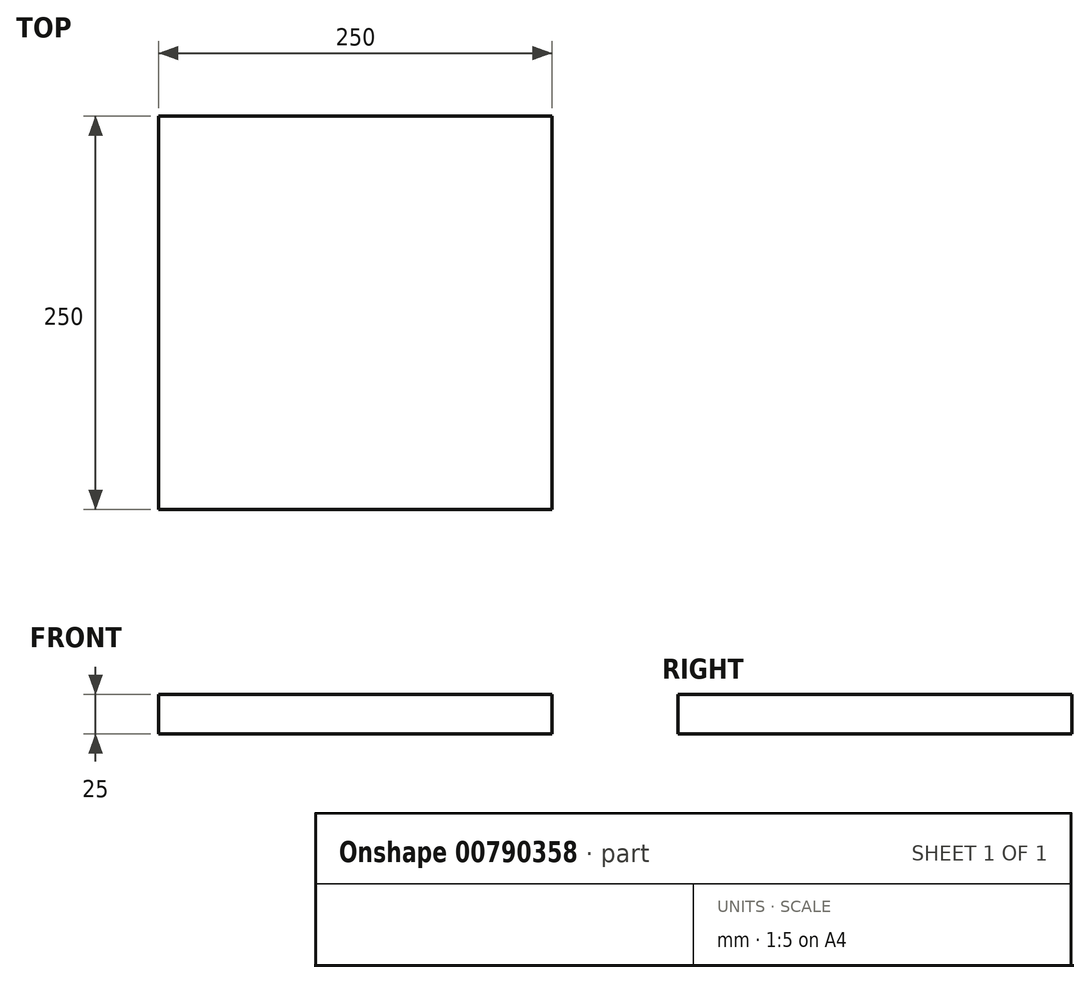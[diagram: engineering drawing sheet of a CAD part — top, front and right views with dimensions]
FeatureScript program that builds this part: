
annotation { "Feature Type Name" : "Feature", "Feature Type Description" : "" }
export const myFeature = defineFeature(function(context is Context, id is Id, definition is map)
    precondition{}
    {
        {
            var Q0;
            Q0=qCreatedBy(makeId("Top.planeOp"),FACE);
            var sketch = newSketch(context, id + "F0", { "sketchPlane" : qUnion([Q0])});
            skLineSegment(sketch, "E0.bottom", {"start": v(125, 125) * mm, "end": v(-125, 125) * mm});
            skLineSegment(sketch, "E0.top", {"start": v(125, -125) * mm, "end": v(-125, -125) * mm});
            skLineSegment(sketch, "E0.left", {"start": v(125, 125) * mm, "end": v(125, -125) * mm});
            skLineSegment(sketch, "E0.right", {"start": v(-125, 125) * mm, "end": v(-125, -125) * mm});
            skPoint(sketch, "E0.middle", {"position": v(0, 0) * mm});
            skSolve(sketch);
        }
        {
            var Q0;
            Q0 = qSketchRegion(id + "F0", true);
            extrude(context, id + "F1", {"entities" : qUnion([Q0]), "depth" : 25 * mm, "offsetDistance" : 25 * mm});
        }
    });
